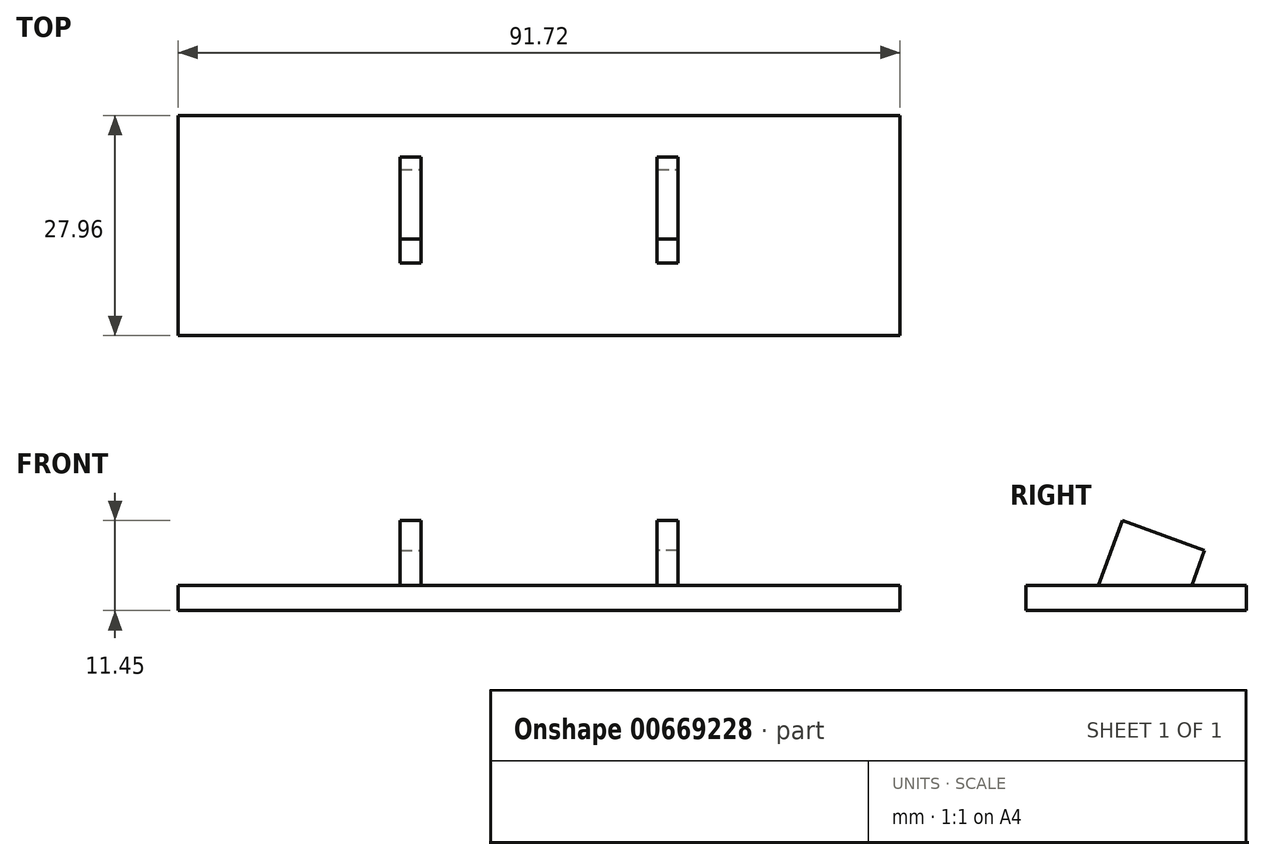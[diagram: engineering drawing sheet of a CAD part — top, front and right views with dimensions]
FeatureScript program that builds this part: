
annotation { "Feature Type Name" : "Feature", "Feature Type Description" : "" }
export const myFeature = defineFeature(function(context is Context, id is Id, definition is map)
    precondition{}
    {
        {
            var Q0;
            Q0=qCreatedBy(makeId("Top.planeOp"),FACE);
            var sketch = newSketch(context, id + "F0", { "sketchPlane" : qUnion([Q0])});
            skLineSegment(sketch, "E0.bottom", {"start": v(45.86, -13.98) * mm, "end": v(-45.86, -13.98) * mm});
            skLineSegment(sketch, "E0.top", {"start": v(45.86, 13.98) * mm, "end": v(-45.86, 13.98) * mm});
            skLineSegment(sketch, "E0.left", {"start": v(45.86, -13.98) * mm, "end": v(45.86, 13.98) * mm});
            skLineSegment(sketch, "E0.right", {"start": v(-45.86, -13.98) * mm, "end": v(-45.86, 13.98) * mm});
            skPoint(sketch, "E0.middle", {"position": v(0, 0) * mm});
            skSolve(sketch);
        }
        {
            var Q0;
            Q0=makeQuery(id+"F0.imprint","IMPRINT",FACE,{"disambiguationData":[TD([[makeQuery(id+"F0.imprint","IMPRINT",EDGE,{"derivedFrom":sQuery(id+"F0.wireOp",EDGE,"E0.bottom")}),-1.0]])]});
            extrude(context, id + "F1", {"entities" : qUnion([Q0]), "depth" : 3.17 * mm, "offsetDistance" : 25.4 * mm});
        }
        {
            var Q0;
            Q0=qCreatedBy(makeId("Top.planeOp"),FACE);
            var sketch = newSketch(context, id + "F2", { "sketchPlane" : qUnion([Q0])});
            skLineSegment(sketch, "E1", {"start": v(0, 0) * mm, "end": v(17.44, 0) * mm, "construction": true});
            skSolve(sketch);
        }
        {
            var Q0;
            Q0=sQuery(id+"F2.wireOp",EDGE,"E1");
            cPlane(context, id + "F3", {"entities" : qUnion([Q0]), "cplaneType" : CPlaneType.LINE_ANGLE, "offset" : 25.4 * mm, "angle" : 70 * degree, "width" : 152.4 * mm, "height" : 152.4 * mm});
        }
        {
            var Q0;
            Q0=qCreatedBy(id+"F3.planeOp",FACE);
            var sketch = newSketch(context, id + "F4", { "sketchPlane" : qUnion([Q0])});
            skLineSegment(sketch, "E2.bottom", {"start": v(17.64, -5.56) * mm, "end": v(14.97, -5.56) * mm});
            skLineSegment(sketch, "E2.top", {"start": v(17.64, 5.56) * mm, "end": v(14.97, 5.56) * mm});
            skLineSegment(sketch, "E2.left", {"start": v(17.64, -5.56) * mm, "end": v(17.64, 5.56) * mm});
            skLineSegment(sketch, "E2.right", {"start": v(14.97, -5.56) * mm, "end": v(14.97, 5.56) * mm});
            skPoint(sketch, "E2.middle", {"position": v(16.3, 0) * mm});
            skSolve(sketch);
        }
        {
            var Q0;
            Q0 = qSketchRegion(id + "F4", true);
            extrude(context, id + "F5", {"entities" : qUnion([Q0]), "depth" : 10.16 * mm, "offsetDistance" : 25.4 * mm});
        }
        {
            var Q0;
            Q0=makeQuery(id+"F5.opExtrude","SWEPT_BODY",BODY,{"disambiguationData":[OSD([sQuery(id+"F4.wireOp",EDGE,"E2.bottom"),sQuery(id+"F4.wireOp",EDGE,"E2.top"),sQuery(id+"F4.wireOp",EDGE,"E2.left"),sQuery(id+"F4.wireOp",EDGE,"E2.right")])]});
            var Q1;
            Q1=qCreatedBy(makeId("Right.planeOp"),FACE);
            mirror(context, id + "F6", {"operationType" : NewBodyOperationType.ADD, "entities" : qUnion([Q0]), "mirrorPlane" : qUnion([Q1])});
        }
        {
            var Q0;
            Q0=qCreatedBy(makeId("Right.planeOp"),FACE);
            var sketch = newSketch(context, id + "F7", { "sketchPlane" : qUnion([Q0])});
            skLineSegment(sketch, "E3.bottom", {"start": v(-17.91, 0) * mm, "end": v(18.36, 0) * mm});
            skLineSegment(sketch, "E3.top", {"start": v(-17.91, -13.6) * mm, "end": v(18.36, -13.6) * mm});
            skLineSegment(sketch, "E3.left", {"start": v(-17.91, 0) * mm, "end": v(-17.91, -13.6) * mm});
            skLineSegment(sketch, "E3.right", {"start": v(18.36, 0) * mm, "end": v(18.36, -13.6) * mm});
            skSolve(sketch);
        }
        {
            var Q0;
            Q0 = qSketchRegion(id + "F7", true);
            extrude(context, id + "F8", {"entities" : qUnion([Q0]), "operationType" : NewBodyOperationType.REMOVE, "endBound" : BoundingType.SYMMETRIC, "depth" : 136.14 * mm, "offsetDistance" : 25.4 * mm});
        }
    });
